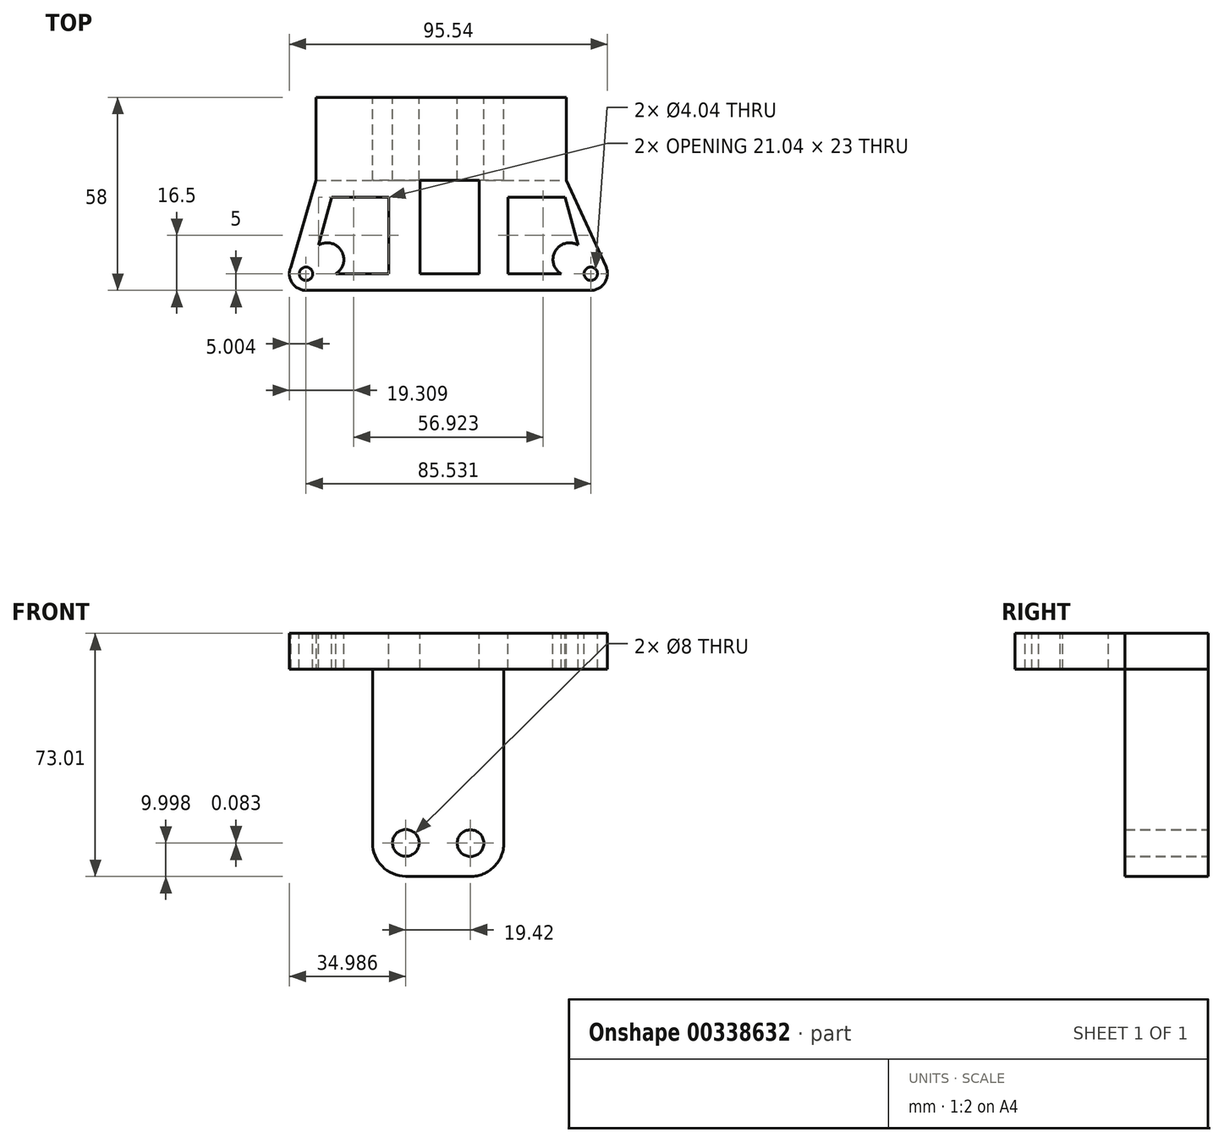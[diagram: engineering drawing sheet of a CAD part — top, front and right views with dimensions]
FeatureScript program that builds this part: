
annotation { "Feature Type Name" : "Feature", "Feature Type Description" : "" }
export const myFeature = defineFeature(function(context is Context, id is Id, definition is map)
    precondition{}
    {
        {
            var Q0;
            Q0=qCreatedBy(makeId("Front.planeOp"),FACE);
            var sketch = newSketch(context, id + "F0", { "sketchPlane" : qUnion([Q0])});
            skLineSegment(sketch, "E0", {"start": v(-22.78, 0) * mm, "end": v(-22.78, -52.17) * mm});
            skPoint(sketch, "E1.visualSharp", {"position": v(-22.78, -62.17) * mm});
            skArc(sketch, "E1.filletArc", {"start": v(-22.78, -52.17) * mm, "mid": v(-19.86, -59.24) * mm, "end": v(-12.78, -62.17) * mm});
            skCircle(sketch, "E2", {"center": v(-12.78, -52.17) * mm, "radius": 4 * mm});
            skLineSegment(sketch, "E3", {"start": v(-6.15, 0) * mm, "end": v(-6.15, -62.17) * mm});
            skLineSegment(sketch, "E4", {"start": v(-0.15, 0) * mm, "end": v(-0.15, -62.17) * mm});
            skPoint(sketch, "E4.endSnap0", {"position": v(0, -62.17) * mm});
            skLineSegment(sketch, "E5", {"start": v(16.64, 0) * mm, "end": v(16.64, -52.25) * mm});
            skLineSegment(sketch, "E6", {"start": v(-12.78, -62.17) * mm, "end": v(6.6, -62.25) * mm});
            skPoint(sketch, "E7.visualSharp", {"position": v(16.64, -62.3) * mm});
            skArc(sketch, "E7.filletArc", {"start": v(6.6, -62.25) * mm, "mid": v(13.7, -59.34) * mm, "end": v(16.64, -52.25) * mm});
            skCircle(sketch, "E8", {"center": v(6.64, -52.25) * mm, "radius": 4 * mm});
            skLineSegment(sketch, "E9", {"start": v(-39.78, 0) * mm, "end": v(35.44, 0) * mm});
            skLineSegment(sketch, "E10", {"start": v(35.44, 0) * mm, "end": v(35.44, 10.76) * mm});
            skLineSegment(sketch, "E11", {"start": v(35.44, 10.76) * mm, "end": v(-39.78, 10.76) * mm});
            skLineSegment(sketch, "E12", {"start": v(-39.78, 10.76) * mm, "end": v(-39.78, 0) * mm});
            skLineSegment(sketch, "E13", {"start": v(-31.1, 10.76) * mm, "end": v(-31.1, 0) * mm});
            skLineSegment(sketch, "E14", {"start": v(27.12, 10.76) * mm, "end": v(27.12, 0) * mm});
            skSolve(sketch);
        }
        {
            var Q0;
            Q0 = qSketchRegion(id + "F0", true);
            extrude(context, id + "F1", {"entities" : qUnion([Q0]), "depth" : 25 * mm});
        }
        {
            var Q0;
            Q0=makeQuery(id+"F1.opExtrude","SWEPT_FACE",FACE,{"disambiguationData":[OSD([sQuery(id+"F0.wireOp",EDGE,"E11")])]});
            var sketch = newSketch(context, id + "F2", { "sketchPlane" : qUnion([Q0])});
            skLineSegment(sketch, "E15", {"start": v(35.44, -25) * mm, "end": v(9.3, -25) * mm});
            skLineSegment(sketch, "E16", {"start": v(9.3, -25) * mm, "end": v(9.3, -53) * mm});
            skLineSegment(sketch, "E17", {"start": v(9.3, -53) * mm, "end": v(-8.55, -53) * mm});
            skLineSegment(sketch, "E18", {"start": v(-8.55, -53) * mm, "end": v(-8.55, -25) * mm});
            skLineSegment(sketch, "E19", {"start": v(-8.55, -25) * mm, "end": v(-39.78, -25) * mm});
            skLineSegment(sketch, "E20.MirrorCS", {"start": v(-17.94, -30) * mm, "end": v(-17.94, -53) * mm});
            skLineSegment(sketch, "E21.MirrorCS", {"start": v(-35.08, -30) * mm, "end": v(-17.94, -30) * mm});
            skLineSegment(sketch, "E22.MirrorCS", {"start": v(-35.08, -30) * mm, "end": v(-38.98, -44.43) * mm});
            skLineSegment(sketch, "E23.MirrorCS", {"start": v(-17.94, -53) * mm, "end": v(-33.84, -53) * mm});
            skArc(sketch, "E24.MirrorCS", {"start": v(-38.98, -44.43) * mm, "mid": v(-32.12, -46.14) * mm, "end": v(-33.84, -53) * mm});
            skLineSegment(sketch, "E25.MirrorCS", {"start": v(-42.77, -58) * mm, "end": v(0, -58) * mm});
            skArc(sketch, "E26.MirrorCS", {"start": v(-42.77, -58) * mm, "mid": v(-46.97, -55.7) * mm, "end": v(-47.31, -50.92) * mm});
            skCircle(sketch, "E27.MirrorC", {"center": v(-42.77, -53) * mm, "radius": 2.02 * mm});
            skLineSegment(sketch, "E28", {"start": v(-39.78, -25) * mm, "end": v(-47.31, -50.92) * mm});
            skLineSegment(sketch, "E29.MirrorCS", {"start": v(17.94, -30) * mm, "end": v(17.94, -53) * mm});
            skLineSegment(sketch, "E30.MirrorCS", {"start": v(35.08, -30) * mm, "end": v(17.94, -30) * mm});
            skLineSegment(sketch, "E31.MirrorCS", {"start": v(35.08, -30) * mm, "end": v(38.98, -44.43) * mm});
            skArc(sketch, "E32.MirrorCS", {"start": v(38.98, -44.43) * mm, "mid": v(32.12, -46.14) * mm, "end": v(33.84, -53) * mm});
            skLineSegment(sketch, "E33.MirrorCS", {"start": v(42.77, -58) * mm, "end": v(0, -58) * mm});
            skArc(sketch, "E34.MirrorCS", {"start": v(42.77, -58) * mm, "mid": v(46.97, -55.7) * mm, "end": v(47.31, -50.92) * mm});
            skLineSegment(sketch, "E35", {"start": v(47.31, -50.92) * mm, "end": v(35.44, -25) * mm});
            skCircle(sketch, "E36.MirrorC", {"center": v(42.77, -53) * mm, "radius": 2.02 * mm});
            skLineSegment(sketch, "E37.MirrorCS", {"start": v(17.94, -53) * mm, "end": v(33.84, -53) * mm});
            skSolve(sketch);
        }
        {
            var Q0;
            Q0 = qSketchRegion(id + "F2", true);
            extrude(context, id + "F3", {"entities" : qUnion([Q0]), "operationType" : NewBodyOperationType.ADD, "oppositeDirection" : true, "depth" : 10.8 * mm});
        }
    });
